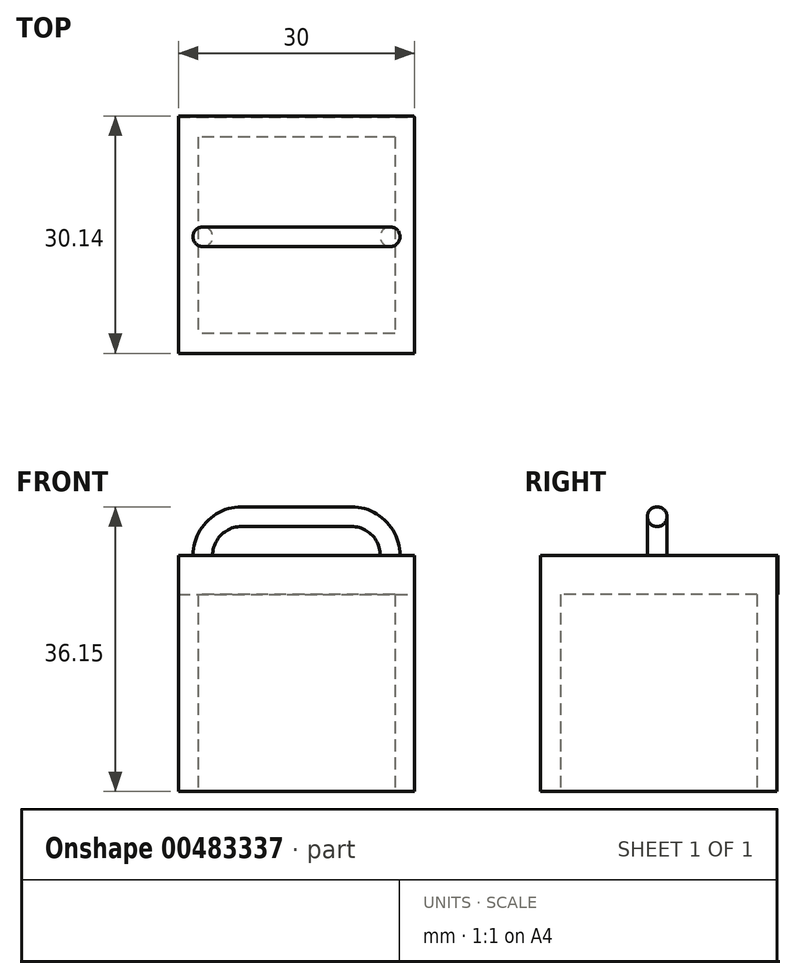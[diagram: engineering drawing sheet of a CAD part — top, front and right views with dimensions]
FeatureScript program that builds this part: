
annotation { "Feature Type Name" : "Feature", "Feature Type Description" : "" }
export const myFeature = defineFeature(function(context is Context, id is Id, definition is map)
    precondition{}
    {
        {
            var Q0;
            Q0=qCreatedBy(makeId("Top.planeOp"),FACE);
            var sketch = newSketch(context, id + "F0", { "sketchPlane" : qUnion([Q0])});
            skLineSegment(sketch, "E0.bottom", {"start": v(0, 0) * mm, "end": v(30, 0) * mm});
            skLineSegment(sketch, "E0.top", {"start": v(0, 30) * mm, "end": v(30, 30) * mm});
            skLineSegment(sketch, "E0.left", {"start": v(0, 0) * mm, "end": v(0, 30) * mm});
            skLineSegment(sketch, "E0.right", {"start": v(30, 0) * mm, "end": v(30, 30) * mm});
            skSolve(sketch);
        }
        {
            var Q0;
            Q0 = qSketchRegion(id + "F0", true);
            extrude(context, id + "F1", {"entities" : qUnion([Q0]), "depth" : 30 * mm});
        }
        {
            var Q0;
            Q0=makeQuery(id+"F1.opExtrude","CAP_FACE",FACE,{"disambiguationData":[OSD([sQuery(id+"F0.wireOp",EDGE,"E0.bottom"),sQuery(id+"F0.wireOp",EDGE,"E0.top"),sQuery(id+"F0.wireOp",EDGE,"E0.left"),sQuery(id+"F0.wireOp",EDGE,"E0.right")])],"isStart":false});
            var sketch = newSketch(context, id + "F2", { "sketchPlane" : qUnion([Q0])});
            skLineSegment(sketch, "E1", {"start": v(0, 15) * mm, "end": v(30, 15) * mm, "construction": true});
            skSolve(sketch);
        }
        {
            var Q0;
            Q0=sQuery(id+"F2.wireOp",EDGE,"E1");
            var Q1;
            Q1=makeQuery(id+"F2.imprint","IMPRINT",FACE,{"disambiguationData":[TD([[makeQuery(id+"F2.imprint","IMPRINT",EDGE,{"derivedFrom":makeQuery(id+"F1.opExtrude","CAP_EDGE",EDGE,{"disambiguationData":[OSD([sQuery(id+"F0.wireOp",EDGE,"E0.bottom")])],"isStart":false})}),1.0]])]});
            cPlane(context, id + "F3", {"entities" : qUnion([Q0, Q1]), "cplaneType" : CPlaneType.LINE_ANGLE, "offset" : 25 * mm, "angle" : 90 * degree, "width" : 150 * mm, "height" : 150 * mm});
        }
        {
            var Q0;
            Q0=qCreatedBy(id+"F3.planeOp",FACE);
            var sketch = newSketch(context, id + "F4", { "sketchPlane" : qUnion([Q0])});
            skArc(sketch, "E2", {"start": v(-22, 35) * mm, "mid": v(-25.54, 33.54) * mm, "end": v(-27, 30) * mm});
            skArc(sketch, "E3", {"start": v(-3, 30) * mm, "mid": v(-4.46, 33.54) * mm, "end": v(-8, 35) * mm});
            skLineSegment(sketch, "E4", {"start": v(-22, 35) * mm, "end": v(-8, 35) * mm});
            skSolve(sketch);
        }
        {
            var Q0;
            Q0=makeQuery(id+"F2.imprint","IMPRINT",FACE,{"disambiguationData":[TD([[makeQuery(id+"F2.imprint","IMPRINT",EDGE,{"derivedFrom":makeQuery(id+"F1.opExtrude","CAP_EDGE",EDGE,{"disambiguationData":[OSD([sQuery(id+"F0.wireOp",EDGE,"E0.bottom")])],"isStart":false})}),1.0]])]});
            var sketch = newSketch(context, id + "F5", { "sketchPlane" : qUnion([Q0])});
            skCircle(sketch, "E5", {"center": v(26.9, 14.81) * mm, "radius": 1.25 * mm});
            skSolve(sketch);
        }
        {
            var Q0;
            Q0=makeQuery(id+"F5.imprint","IMPRINT",FACE,{"disambiguationData":[TD([[makeQuery(id+"F5.imprint","IMPRINT",EDGE,{"derivedFrom":sQuery(id+"F5.wireOp",EDGE,"E5")}),1.0]])]});
            var Q1;
            Q1 = qConstructionFilter(qBodyType(qCreatedBy(id + "F4" ,EDGE), BodyType.WIRE), ConstructionObject.NO);
            sweep(context, id + "F6", {"operationType" : NewBodyOperationType.ADD, "profiles" : qUnion([Q0]), "path" : qUnion([Q1])});
        }
        {
            var Q0;
            Q0=makeQuery(id+"F1.opExtrude","CAP_FACE",FACE,{"disambiguationData":[OSD([sQuery(id+"F0.wireOp",EDGE,"E0.bottom"),sQuery(id+"F0.wireOp",EDGE,"E0.top"),sQuery(id+"F0.wireOp",EDGE,"E0.left"),sQuery(id+"F0.wireOp",EDGE,"E0.right")])],"isStart":true});
            var sketch = newSketch(context, id + "F7", { "sketchPlane" : qUnion([Q0])});
            skLineSegment(sketch, "E6.bottom", {"start": v(27.5, -27.5) * mm, "end": v(2.5, -27.5) * mm});
            skLineSegment(sketch, "E6.top", {"start": v(27.5, -2.5) * mm, "end": v(2.5, -2.5) * mm});
            skLineSegment(sketch, "E6.left", {"start": v(27.5, -27.5) * mm, "end": v(27.5, -2.5) * mm});
            skLineSegment(sketch, "E6.right", {"start": v(2.5, -27.5) * mm, "end": v(2.5, -2.5) * mm});
            skPoint(sketch, "E6.middle", {"position": v(15, -15) * mm});
            skLineSegment(sketch, "E7", {"start": v(15, -15) * mm, "end": v(15, 0) * mm, "construction": true});
            skLineSegment(sketch, "E8", {"start": v(15, -15) * mm, "end": v(0, -15) * mm, "construction": true});
            skSolve(sketch);
        }
        {
            var Q0;
            Q0=makeQuery(id+"F7.imprint","IMPRINT",FACE,{"disambiguationData":[TD([[makeQuery(id+"F7.imprint","IMPRINT",EDGE,{"derivedFrom":sQuery(id+"F7.wireOp",EDGE,"E6.bottom")}),-1.0]])]});
            var Q1;
            Q1=makeQuery(id+"F1.opExtrude","CAP_FACE",FACE,{"disambiguationData":[OSD([sQuery(id+"F0.wireOp",EDGE,"E0.bottom"),sQuery(id+"F0.wireOp",EDGE,"E0.top"),sQuery(id+"F0.wireOp",EDGE,"E0.left"),sQuery(id+"F0.wireOp",EDGE,"E0.right")])],"isStart":false});
            extrude(context, id + "F8", {"entities" : qUnion([Q0]), "operationType" : NewBodyOperationType.REMOVE, "endBound" : BoundingType.UP_TO_SURFACE, "oppositeDirection" : true, "endBoundEntityFace" : qUnion([Q1]), "depth" : 25 * mm});
        }
        {
            var Q0;
            Q0=makeQuery(id+"F2.imprint","IMPRINT",FACE,{"disambiguationData":[TD([[makeQuery(id+"F2.imprint","IMPRINT",EDGE,{"derivedFrom":makeQuery(id+"F1.opExtrude","CAP_EDGE",EDGE,{"disambiguationData":[OSD([sQuery(id+"F0.wireOp",EDGE,"E0.bottom")])],"isStart":false})}),1.0]])]});
            var sketch = newSketch(context, id + "F9", { "sketchPlane" : qUnion([Q0])});
            skLineSegment(sketch, "E9.bottom", {"start": v(0, 30.14) * mm, "end": v(29.94, 30.14) * mm});
            skLineSegment(sketch, "E9.top", {"start": v(0, 0) * mm, "end": v(29.94, 0) * mm});
            skLineSegment(sketch, "E9.left", {"start": v(0, 30.14) * mm, "end": v(0, 0) * mm});
            skLineSegment(sketch, "E9.right", {"start": v(29.94, 30.14) * mm, "end": v(29.94, 0) * mm});
            skSolve(sketch);
        }
        {
            var Q0;
            Q0 = qSketchRegion(id + "F9", true);
            extrude(context, id + "F10", {"entities" : qUnion([Q0]), "operationType" : NewBodyOperationType.ADD, "oppositeDirection" : true, "depth" : 5 * mm});
        }
    });
